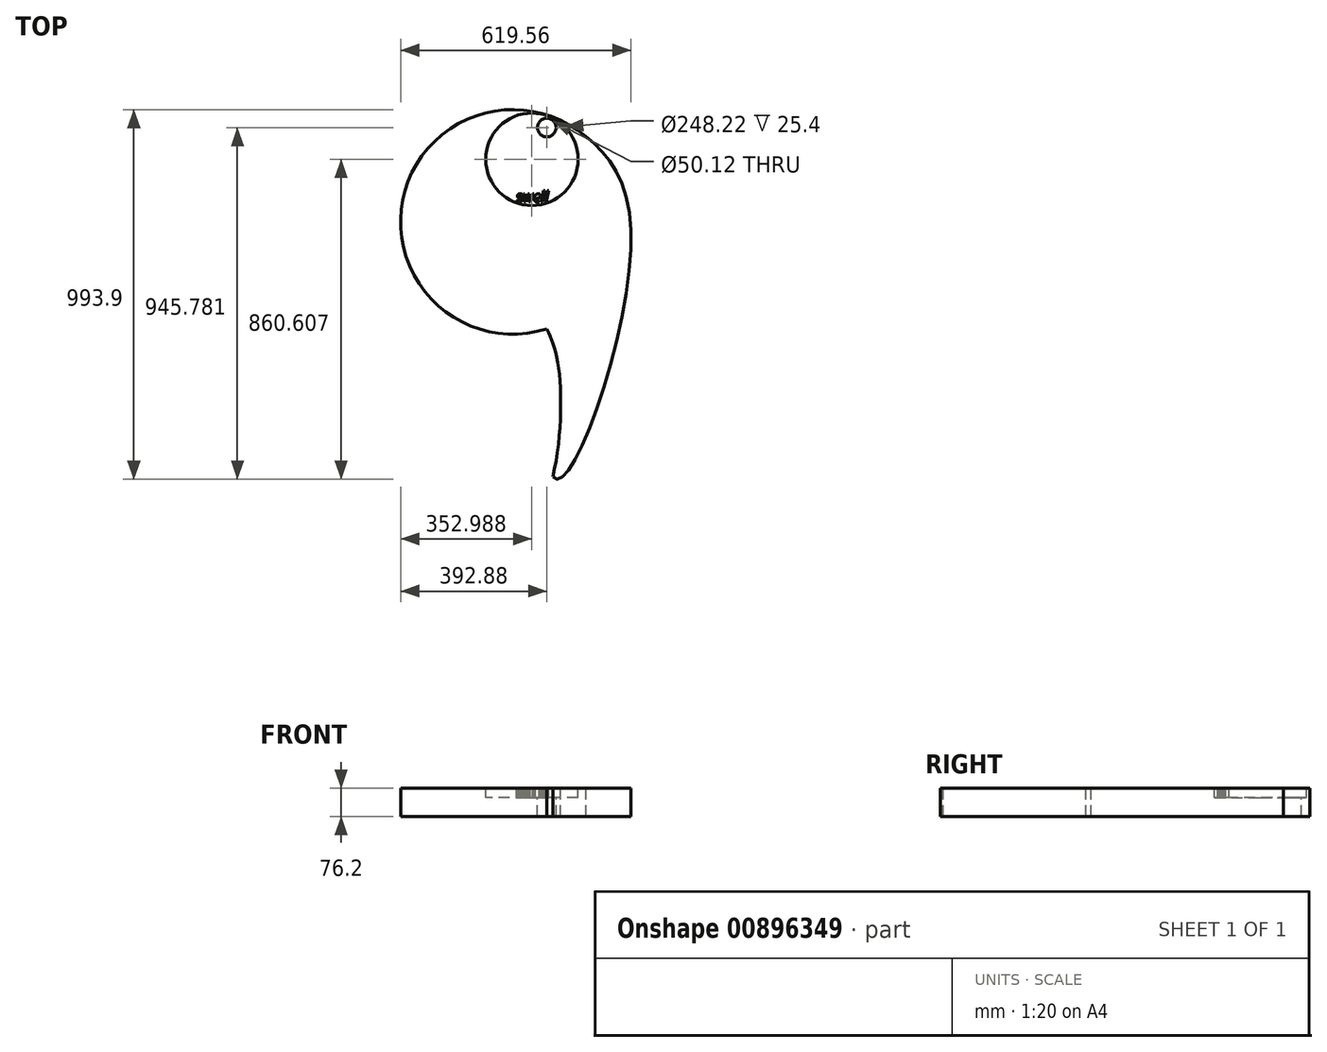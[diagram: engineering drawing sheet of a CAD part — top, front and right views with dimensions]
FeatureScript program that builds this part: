
annotation { "Feature Type Name" : "Feature", "Feature Type Description" : "" }
export const myFeature = defineFeature(function(context is Context, id is Id, definition is map)
    precondition{}
    {
        {
            var Q0;
            Q0=qCreatedBy(makeId("Top.planeOp"),FACE);
            var sketch = newSketch(context, id + "F0", { "sketchPlane" : qUnion([Q0])});
            skArc(sketch, "E0", {"start": v(103.64, 518.17) * mm, "mid": v(-387.02, 346.85) * mm, "end": v(0, 0) * mm});
            skFitSpline(sketch, "E1", {"points": [v(46.5, 556.22) * mm, v(226.61, 252.36) * mm, v(16.3, -397.66) * mm], "startDerivative": vector(628.6, -374.58) * mm, "endDerivative": vector(-260.42, 353.63) * mm});
            skFitSpline(sketch, "E2", {"points": [v(16.3, -397.66) * mm, v(30.75, -96.8) * mm, v(0, 0) * mm], "startDerivative": vector(113.75, 482.81) * mm, "endDerivative": vector(-109.05, 221.08) * mm});
            skSolve(sketch);
        }
        {
            var Q0;
            Q0 = qSketchRegion(id + "F0", true);
            extrude(context, id + "F1", {"entities" : qUnion([Q0]), "depth" : 76.2 * mm, "offsetDistance" : 25.4 * mm});
        }
        {
            var Q0;
            Q0=makeQuery(id+"F1.opExtrude","CAP_FACE",FACE,{"disambiguationData":[OSD([sQuery(id+"F0.wireOp",EDGE,"E0"),sQuery(id+"F0.wireOp",EDGE,"E1"),sQuery(id+"F0.wireOp",EDGE,"E2")])],"isStart":false});
            var sketch = newSketch(context, id + "F2", { "sketchPlane" : qUnion([Q0])});
            skCircle(sketch, "E3", {"center": v(-39.9, 456.14) * mm, "radius": 124.11 * mm});
            skText(sketch, "E4", { "text": "swell", "fontName": "OpenSans-Italic.ttf"});
            skCircle(sketch, "E5", {"center": v(0, 541.31) * mm, "radius": 25.06 * mm});
            const initialGuessF2  = {"E4": [-0.08172, 0.3415, 1, 0, 0.02888]};
            skSetInitialGuess(sketch, initialGuessF2);
            skSolve(sketch);
        }
        {
            var Q0;
            Q0 = qSketchRegion(id + "F2", true);
            var Q1;
            Q1=makeQuery(id+"F2.imprint","IMPRINT",FACE,{"disambiguationData":[TD([[makeQuery(id+"F2.imprint","IMPRINT",EDGE,{"derivedFrom":sQuery(id+"F2.wireOp",EDGE,"E5")}),1.0]])]});
            extrude(context, id + "F3", {"entities" : qUnion([Q0, Q1]), "operationType" : NewBodyOperationType.REMOVE, "oppositeDirection" : true, "depth" : 25.4 * mm, "offsetDistance" : 25.4 * mm});
        }
        {
            var Q0;
            Q0=makeQuery(id+"F2.imprint","IMPRINT",FACE,{"disambiguationData":[TD([[makeQuery(id+"F2.imprint","IMPRINT",EDGE,{"derivedFrom":sQuery(id+"F2.wireOp",EDGE,"E5")}),1.0]])]});
            var Q1;
            Q1=sQuery(id+"F2.wireOp",EDGE,"E5");
            extrude(context, id + "F4", {"entities" : qUnion([Q0]), "operationType" : NewBodyOperationType.REMOVE, "surfaceEntities" : qUnion([Q1]), "endBound" : BoundingType.THROUGH_ALL, "oppositeDirection" : true, "depth" : 231.14 * mm, "offsetDistance" : 25.4 * mm});
        }
    });
